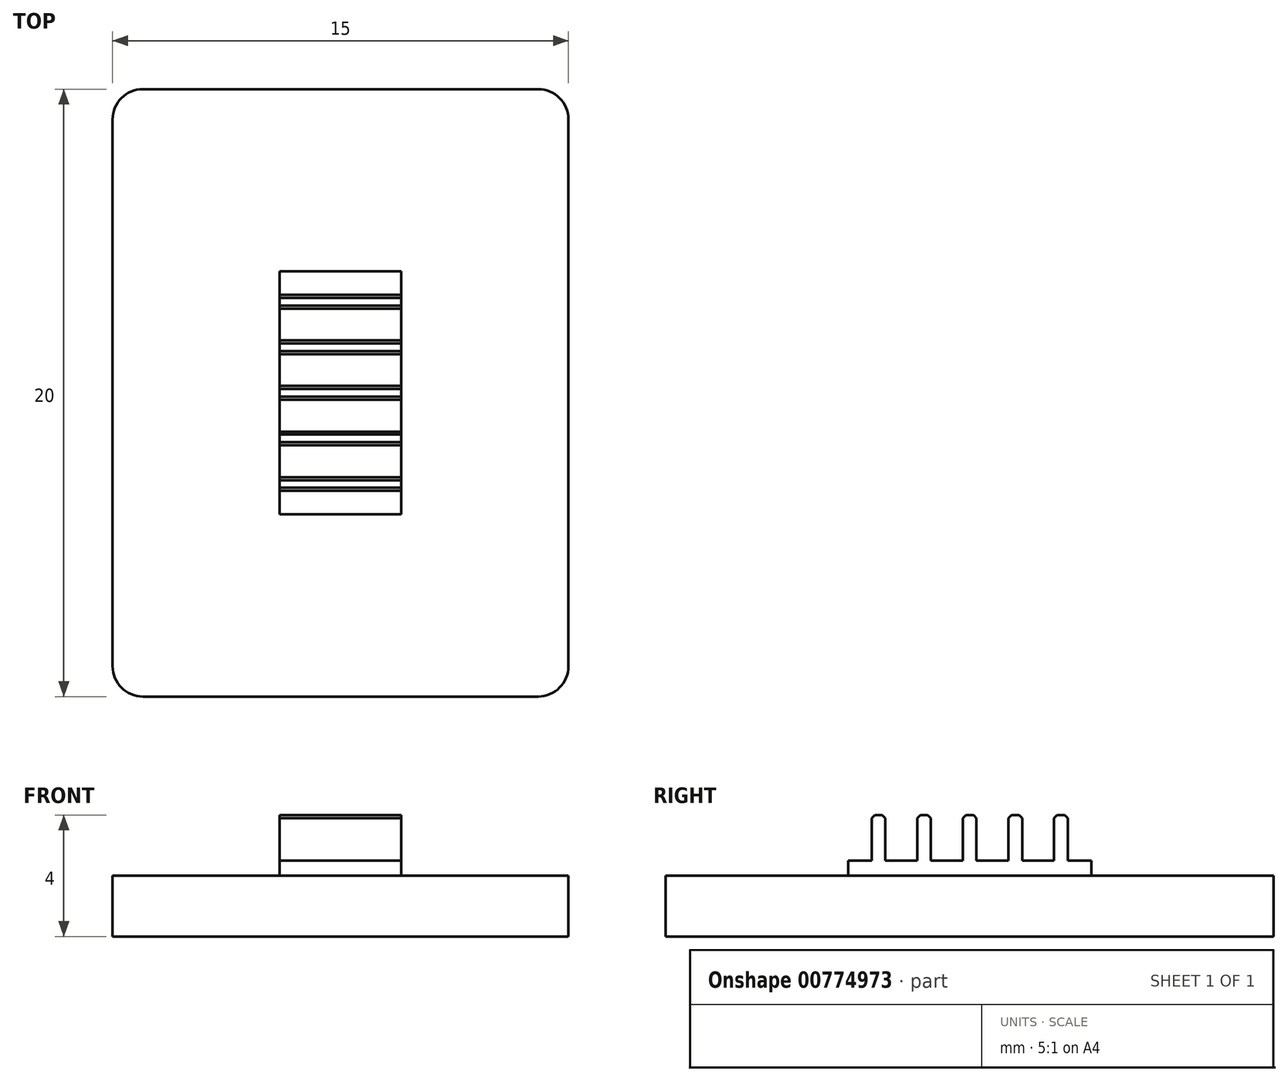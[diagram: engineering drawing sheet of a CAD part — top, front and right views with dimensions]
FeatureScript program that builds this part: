
annotation { "Feature Type Name" : "Feature", "Feature Type Description" : "" }
export const myFeature = defineFeature(function(context is Context, id is Id, definition is map)
    precondition{}
    {
        {
            var Q0;
            Q0=qCreatedBy(makeId("Top.planeOp"),FACE);
            var sketch = newSketch(context, id + "F0", { "sketchPlane" : qUnion([Q0])});
            skLineSegment(sketch, "E0.bottom", {"start": v(7.5, -10) * mm, "end": v(-7.5, -10) * mm});
            skLineSegment(sketch, "E0.top", {"start": v(7.5, 10) * mm, "end": v(-7.5, 10) * mm});
            skLineSegment(sketch, "E0.left", {"start": v(7.5, -10) * mm, "end": v(7.5, 10) * mm});
            skLineSegment(sketch, "E0.right", {"start": v(-7.5, -10) * mm, "end": v(-7.5, 10) * mm});
            skPoint(sketch, "E0.middle", {"position": v(0, 0) * mm});
            skLineSegment(sketch, "E1.bottom", {"start": v(2, -4) * mm, "end": v(-2, -4) * mm});
            skLineSegment(sketch, "E1.top", {"start": v(2, 4) * mm, "end": v(-2, 4) * mm});
            skLineSegment(sketch, "E1.left", {"start": v(2, -4) * mm, "end": v(2, 4) * mm});
            skLineSegment(sketch, "E1.right", {"start": v(-2, -4) * mm, "end": v(-2, 4) * mm});
            skLineSegment(sketch, "E2", {"start": v(-2, 0.1) * mm, "end": v(-2, 0) * mm});
            skPoint(sketch, "E3", {"position": v(0, 1.5) * mm});
            skPoint(sketch, "E4", {"position": v(0, -1.5) * mm});
            skLineSegment(sketch, "E5.bottom", {"start": v(2, -0.23) * mm, "end": v(-2, -0.23) * mm});
            skLineSegment(sketch, "E5.top", {"start": v(2, 0.23) * mm, "end": v(-2, 0.23) * mm});
            skLineSegment(sketch, "E5.left", {"start": v(2, -0.23) * mm, "end": v(2, 0.23) * mm});
            skLineSegment(sketch, "E5.right", {"start": v(-2, -0.23) * mm, "end": v(-2, 0.23) * mm});
            skLineSegment(sketch, "E6.bottom", {"start": v(2, 1.28) * mm, "end": v(-2, 1.28) * mm});
            skLineSegment(sketch, "E6.top", {"start": v(2, 1.72) * mm, "end": v(-2, 1.72) * mm});
            skLineSegment(sketch, "E6.left", {"start": v(2, 1.28) * mm, "end": v(2, 1.72) * mm});
            skLineSegment(sketch, "E6.right", {"start": v(-2, 1.28) * mm, "end": v(-2, 1.72) * mm});
            skLineSegment(sketch, "E7.bottom", {"start": v(2, -1.72) * mm, "end": v(-2, -1.72) * mm});
            skLineSegment(sketch, "E7.top", {"start": v(2, -1.27) * mm, "end": v(-2, -1.27) * mm});
            skLineSegment(sketch, "E7.left", {"start": v(2, -1.72) * mm, "end": v(2, -1.27) * mm});
            skLineSegment(sketch, "E7.right", {"start": v(-2, -1.72) * mm, "end": v(-2, -1.27) * mm});
            skPoint(sketch, "E8", {"position": v(0, 3) * mm});
            skPoint(sketch, "E8.positionSnap0", {"position": v(0, 1.28) * mm});
            skPoint(sketch, "E9", {"position": v(0, -3) * mm});
            skLineSegment(sketch, "E10.bottom", {"start": v(2, -3.23) * mm, "end": v(-2, -3.23) * mm});
            skLineSegment(sketch, "E10.top", {"start": v(2, -2.78) * mm, "end": v(-2, -2.78) * mm});
            skLineSegment(sketch, "E10.left", {"start": v(2, -3.23) * mm, "end": v(2, -2.78) * mm});
            skLineSegment(sketch, "E10.right", {"start": v(-2, -3.23) * mm, "end": v(-2, -2.78) * mm});
            skLineSegment(sketch, "E11.bottom", {"start": v(2, 2.77) * mm, "end": v(-2, 2.77) * mm});
            skLineSegment(sketch, "E11.top", {"start": v(2, 3.22) * mm, "end": v(-2, 3.22) * mm});
            skLineSegment(sketch, "E11.left", {"start": v(2, 2.77) * mm, "end": v(2, 3.22) * mm});
            skLineSegment(sketch, "E11.right", {"start": v(-2, 2.77) * mm, "end": v(-2, 3.22) * mm});
            skSolve(sketch);
        }
        {
            var Q0;
            Q0=makeQuery(id+"F0.imprint","IMPRINT",FACE,{"disambiguationData":[TD([[makeQuery(id+"F0.imprint","IMPRINT",EDGE,{"derivedFrom":sQuery(id+"F0.wireOp",EDGE,"E0.bottom")}),-1.0]])]});
            extrude(context, id + "F1", {"entities" : qUnion([Q0]), "depth" : 2 * mm, "offsetDistance" : 25 * mm});
        }
        {
            var Q0;
            {var subQ0=sQuery(id+"F0.wireOp",EDGE,"E1.top");Q0=makeQuery(id+"F0.imprint","IMPRINT",FACE,{"disambiguationData":[TD([[makeQuery(id+"F0.imprint","IMPRINT",EDGE,{"derivedFrom":subQ0}),1.0]])]});}
            var Q1;
            {var subQ0=sQuery(id+"F0.wireOp",EDGE,"E5.top");Q1=makeQuery(id+"F0.imprint","IMPRINT",FACE,{"disambiguationData":[TD([[makeQuery(id+"F0.imprint","IMPRINT",EDGE,{"derivedFrom":subQ0}),-1.0]])]});}
            var Q2;
            {var subQ0=sQuery(id+"F0.wireOp",EDGE,"E5.bottom");Q2=makeQuery(id+"F0.imprint","IMPRINT",FACE,{"disambiguationData":[TD([[makeQuery(id+"F0.imprint","IMPRINT",EDGE,{"derivedFrom":subQ0}),1.0]])]});}
            var Q3;
            {var subQ0=sQuery(id+"F0.wireOp",EDGE,"E1.bottom");Q3=makeQuery(id+"F0.imprint","IMPRINT",FACE,{"disambiguationData":[TD([[makeQuery(id+"F0.imprint","IMPRINT",EDGE,{"derivedFrom":subQ0}),-1.0]])]});}
            var Q4;
            {var subQ0=sQuery(id+"F0.wireOp",EDGE,"E6.top");Q4=makeQuery(id+"F0.imprint","IMPRINT",FACE,{"disambiguationData":[TD([[makeQuery(id+"F0.imprint","IMPRINT",EDGE,{"derivedFrom":subQ0}),-1.0]])]});}
            var Q5;
            {var subQ0=sQuery(id+"F0.wireOp",EDGE,"E7.bottom");Q5=makeQuery(id+"F0.imprint","IMPRINT",FACE,{"disambiguationData":[TD([[makeQuery(id+"F0.imprint","IMPRINT",EDGE,{"derivedFrom":subQ0}),1.0]])]});}
            extrude(context, id + "F2", {"entities" : qUnion([Q0, Q1, Q2, Q3, Q4, Q5]), "operationType" : NewBodyOperationType.ADD, "depth" : 2.5 * mm, "offsetDistance" : 25 * mm});
        }
        {
            var Q0;
            Q0=makeQuery(id+"F0.imprint","IMPRINT",FACE,{"disambiguationData":[TD([[makeQuery(id+"F0.imprint","IMPRINT",EDGE,{"derivedFrom":sQuery(id+"F0.wireOp",EDGE,"E6.bottom")}),-1.0]])]});
            var Q1;
            {var subQ1=sQuery(id+"F0.wireOp",EDGE,"E5.bottom");Q1=makeQuery(id+"F0.imprint","IMPRINT",FACE,{"disambiguationData":[TD([[makeQuery(id+"F0.imprint","IMPRINT",EDGE,{"derivedFrom":subQ1}),-1.0]])]});}
            var Q2;
            Q2=makeQuery(id+"F0.imprint","IMPRINT",FACE,{"disambiguationData":[TD([[makeQuery(id+"F0.imprint","IMPRINT",EDGE,{"derivedFrom":sQuery(id+"F0.wireOp",EDGE,"E7.bottom")}),-1.0]])]});
            var Q3;
            Q3=makeQuery(id+"F0.imprint","IMPRINT",FACE,{"disambiguationData":[TD([[makeQuery(id+"F0.imprint","IMPRINT",EDGE,{"derivedFrom":sQuery(id+"F0.wireOp",EDGE,"E11.bottom")}),-1.0]])]});
            var Q4;
            Q4=makeQuery(id+"F0.imprint","IMPRINT",FACE,{"disambiguationData":[TD([[makeQuery(id+"F0.imprint","IMPRINT",EDGE,{"derivedFrom":sQuery(id+"F0.wireOp",EDGE,"E10.bottom")}),-1.0]])]});
            extrude(context, id + "F3", {"entities" : qUnion([Q0, Q1, Q2, Q3, Q4]), "operationType" : NewBodyOperationType.ADD, "depth" : 4 * mm, "offsetDistance" : 25 * mm});
        }
        {
            var Q0;
            Q0=makeQuery(id+"F3.opExtrude","CAP_EDGE",EDGE,{"disambiguationData":[OSD([sQuery(id+"F0.wireOp",EDGE,"E7.bottom")])],"isStart":false});
            var Q1;
            Q1=makeQuery(id+"F3.opExtrude","CAP_EDGE",EDGE,{"disambiguationData":[OSD([sQuery(id+"F0.wireOp",EDGE,"E7.top")])],"isStart":false});
            var Q2;
            Q2=makeQuery(id+"F3.opExtrude","CAP_EDGE",EDGE,{"disambiguationData":[OSD([sQuery(id+"F0.wireOp",EDGE,"E5.bottom")])],"isStart":false});
            var Q3;
            Q3=makeQuery(id+"F3.opExtrude","CAP_EDGE",EDGE,{"disambiguationData":[OSD([sQuery(id+"F0.wireOp",EDGE,"E5.top")])],"isStart":false});
            var Q4;
            Q4=makeQuery(id+"F3.opExtrude","CAP_EDGE",EDGE,{"disambiguationData":[OSD([sQuery(id+"F0.wireOp",EDGE,"E6.bottom")])],"isStart":false});
            var Q5;
            Q5=makeQuery(id+"F3.opExtrude","CAP_EDGE",EDGE,{"disambiguationData":[OSD([sQuery(id+"F0.wireOp",EDGE,"E6.top")])],"isStart":false});
            var Q6;
            Q6=makeQuery(id+"F3.opExtrude","CAP_EDGE",EDGE,{"disambiguationData":[OSD([sQuery(id+"F0.wireOp",EDGE,"E11.bottom")])],"isStart":false});
            var Q7;
            Q7=makeQuery(id+"F3.opExtrude","CAP_EDGE",EDGE,{"disambiguationData":[OSD([sQuery(id+"F0.wireOp",EDGE,"E11.top")])],"isStart":false});
            var Q8;
            Q8=makeQuery(id+"F3.opExtrude","CAP_EDGE",EDGE,{"disambiguationData":[OSD([sQuery(id+"F0.wireOp",EDGE,"E10.bottom")])],"isStart":false});
            var Q9;
            Q9=makeQuery(id+"F3.opExtrude","CAP_EDGE",EDGE,{"disambiguationData":[OSD([sQuery(id+"F0.wireOp",EDGE,"E10.top")])],"isStart":false});
            chamfer(context, id + "F4", {"entities" : qUnion([Q0, Q1, Q2, Q3, Q4, Q5, Q6, Q7, Q8, Q9]), "width" : 0.1 * mm, "tangentPropagation" : true});
        }
        {
            var Q0;
            Q0=makeQuery(id+"F1.opExtrude","SWEPT_EDGE",EDGE,{"disambiguationData":[OSD([sQuery(id+"F0.wireOp",EDGE,"E0.top"),sQuery(id+"F0.wireOp",EDGE,"E0.left")])]});
            var Q1;
            Q1=makeQuery(id+"F1.opExtrude","SWEPT_EDGE",EDGE,{"disambiguationData":[OSD([sQuery(id+"F0.wireOp",EDGE,"E0.bottom"),sQuery(id+"F0.wireOp",EDGE,"E0.left")])]});
            var Q2;
            Q2=makeQuery(id+"F1.opExtrude","SWEPT_EDGE",EDGE,{"disambiguationData":[OSD([sQuery(id+"F0.wireOp",EDGE,"E0.bottom"),sQuery(id+"F0.wireOp",EDGE,"E0.right")])]});
            var Q3;
            Q3=makeQuery(id+"F1.opExtrude","SWEPT_EDGE",EDGE,{"disambiguationData":[OSD([sQuery(id+"F0.wireOp",EDGE,"E0.top"),sQuery(id+"F0.wireOp",EDGE,"E0.right")])]});
            fillet(context, id + "F5", {"entities" : qUnion([Q0, Q1, Q2, Q3]), "radius" : 1 * mm, "tangentPropagation" : true, "allowEdgeOverflow" : false});
        }
    });
